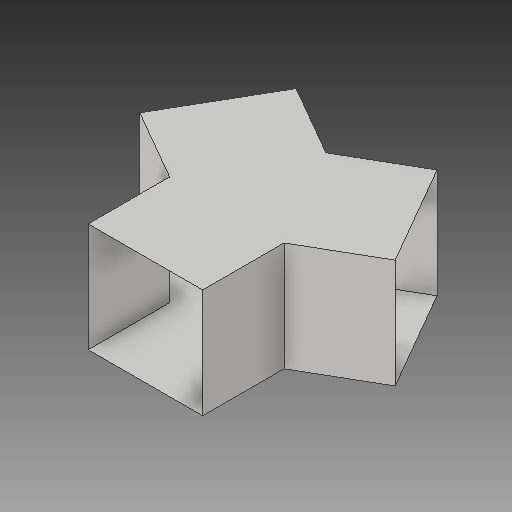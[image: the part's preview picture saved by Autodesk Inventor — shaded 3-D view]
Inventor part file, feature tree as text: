
AUTODESK INVENTOR PART (.ipt)
format: ipt  version: 2017 (Build 210142000, 142)  size: 104,448 bytes
history: native  units: in
note: dims shown in document units (in); Inventor stores cm internally (conversion verified against a paired STEP export)
features: extrude x1, pattern_circular x1, other x1, sketch x1
ambient origin geometry x8: Origin, YZ Plane, XZ Plane, XY Plane, X Axis, Y Axis, Z Axis, Center Point
bodies: Solid1 (feature_tree)
feature tree (4):
  extrude  "corridor"  Depth=6.6667in
  pattern_circular  "made the Y"  [2 undecoded]
  other  "removed ends"
  sketch  "Sketch1"  dims[d0=7.0in d1=6.6667in d2=7.0in d3=0.0in d4=1.1811in d5=360.0deg]
note: 2 required parameter values undecoded (feature->parameter linkage not recoverable at this tier; creation-order binding heuristic only, values carry confidence <= 0.55)
